# Revit family: ledwall-lucia-e_re175-10w-840-wh_715000006600
name_source: partatom
category: Leuchten
revit_build: Autodesk Revit 2016 (Build: 20190508_0715(x64)
units: mm (PartAtom-declared; Revit-internal decimal feet)

## family parameters
Basisbauteil = Fläche
Beim Laden mit Abzugskörper schneiden = Nein
Bemaßung runder Anschluss = Durchmesser verwenden
Gemeinsam genutzt = Nein
Lichtquelle = Nein
Raumberechnungspunkt = Nein
Teiletyp = Normal

## types (1)
- LEDWall-Lucia-E Re175-10W-840-WH (1 x LED, 1000 lm, 4000)
    Approval mark = CE
    Beschreibung = Stylish, compact and sturdy wall mounted fixture for outdoor application. Ultra-slim with only 30mm thickness. Aesthetic up-down lighting effect. Elegant die-casted body design without visible screws . Easy loop-in and loop-out installation. IP65 and suitable for use on coastal applications.
    CIE Flux Codes = 72 91 98 50 100
    Color Rendering = 80
    Color Temperature = 4000
    Control Gear = Electronic ballast
    Frequency = 60 Hz
    Height = 30 mm  [stored 0.0984252 ft]
    Hersteller = OPPLE
    Lamp Light Flux = 1000 lm
    Lamp count = 1
    Lampe = 1 x LED
    Length = 175 mm
    Luminous efficacy = 100 lm/W
    ModVariant = Nein
    Modell = 715000006600
    Mounting Place = Wall
    Mounting Type = Surface mounted
    Number of Poles = 1
    OnlyDefault = Ja
    Power Factor = 1
    Product Name = LEDWall-Lucia-E Re175-10W-840-WH
    Product group = Surface-mounted luminaire
    ProductGroupID = 1
    Protection Class = Protection class I
    Protection Degree = IP 65
    RLX_Detail_Level = 1
    RlxData = <blob elided: 108025 chars, md5=280e7560>
    Scheinlast = 10 VA
    Socket = socket
    Standby Power = 0 W
    System Light Flux = 1000 lm
    System Power = 10 W
    Typenbild = lucia_white_v2.jpg
    Typenkommentare = Product without accessories
    URL = http://relux.com
    VarID = ---
    Voltage = 230 V
    Voltage Range = 220-240 V
    Vorgabe-Ansicht = 1800 mm
    Weight = 0.00 kg
    Width = 90 mm

note: [stored X ft] marks values corroborated as IEEE doubles in the binary element streams (Revit-internal decimal feet)

## geometry (parser evidence)
native form markers: Sweep x13
no freeform markers — native parametric forms only
